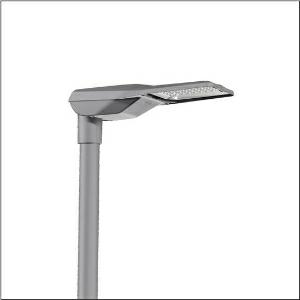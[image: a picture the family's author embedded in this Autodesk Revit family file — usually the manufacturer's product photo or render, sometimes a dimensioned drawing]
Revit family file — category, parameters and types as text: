
# Revit family: streetlight_sl_21_iq_mini___st1_5a_5xe2p41d08gb_b9bd
name_source: partatom
category: Lighting Fixtures
units: mm (PartAtom-declared; Revit-internal decimal feet)

## family parameters
Cut with Voids When Loaded = No
Host = Face
Light Source = No
Part Type = Normal
Room Calculation Point = No
Round Connector Dimension = Use Diameter
Shared = No

## types (1)
- --- (1 x LED, 5810 lm, 37.1 W, 4000K)
    Apparent Load = 37 VA
    CIE Flux Codes = 22 53 95 100 100
    Color Rendering = 70
    Color Temperature = 4000K
    Default Elevation = 1800 mm
    Description = Streetlight SL 21 iQ mini, mast luminaire, primary light control with lens, of PMMA, primary optical cover: cover, of toughened safety glass, transparent, light distribution: ST1.5a, light emission: direct distribution, primary light characteristic: asymmetric, installation type: post-top, side-entry, LED, High Power LED, rated luminous flux: 5.810lm, luminous efficacy: 157lm/W, light colour: 740, colour temperature: 4000K, control gear: iQ-Comfort, control: Auto-Match, Temp-Guard, Lumen-Switch, Night-Set, Smart-Wire, Light-Fading, Desk-Remote (wireless, voltage-free reading and setting of iQ features in the workshop via application-optimized NFC function/RFID function), optimised constant luminous flux control (CLO 2.0), pre-setting: linear dimming characteristic, mains connection: 220..240V, AC, 50/60Hz, start of lifetime: 37W, end of service life: 39W, reduction: 18W, luminaire housing, of diecast aluminium, powder-coated, SITECO metallic grey (DB 702S), corrosivity category C5 high according to DIN EN ISO 12944, please order mast flange separately, inclination adjustable: 0°, 5°, 10°, 15°, sealing non-destructively replaceable, multi-level sealing system, length: 628mm, width: 235mm, height: 110mm, mast flange for spigot size: 42mm (side-entry): 5XC10008XM4, 60/48mm (side-entry/post-top): 5XC10108XM2, 76/60mm (side-entry/post-top): 5XC10108XM1, mounting height: 4..8m, protection rating (complete): IP66, insulation class (complete): insulation class II (safety insulation), certification: CE, ENEC, ENEC+, VDE, impact resistance: IK10, permissible operating ambient temperature for outdoor applications: -40..+50°C, standard-compliant lighting for roads and squares, packaging unit: 1 piece

Light Distribution: ST1.5a
    Height = 110 mm
    Lamp = 1 x LED
    Lamp Light Flux = 5810 lm
    Lamp Power = 37.1 W
    Lamp count = 1
    Length = 625 mm
    Luminous efficacy = 157 lm/W
    Manufacturer = Siteco
    ModVariant = No
    Model = 5XE2P41D08GB
    Number of Poles = 1
    OnlyDefault = Yes
    Power Factor = 1
    Product Name = Streetlight SL 21 iQ mini | ST1.5a
    Product group = mast luminaire | pylon top
    ProductGroupID = 6100
    Protection Class = Protection class II
    Protection Degree = IP 66
    RLX_Detail_Level = 1
    RLX_Emergency_Light_Flux = 0 lm
    RLX_Emergency_Type = 0
    RLX_Emergency_Type_DB = No
    RlxData = <blob elided: 29989 chars, md5=8d5bec8d>
    Socket = socket
    Standby Power = 0 W
    System Light Flux = 5810 lm
    System Power = 37 W
    Type Comments = factory setting: luminous flux: 100 % | dim-lin: 254 | 385 mA
    Type Image = l_1003519.jpg
    URL = http://relux.com
    VarID = @adj_175275
    Voltage = 0 V
    Weight = 0.00 kg
    Width = 234 mm

## geometry (parser evidence)
native form markers: Blend x4, Sweep x12
no freeform markers — native parametric forms only
